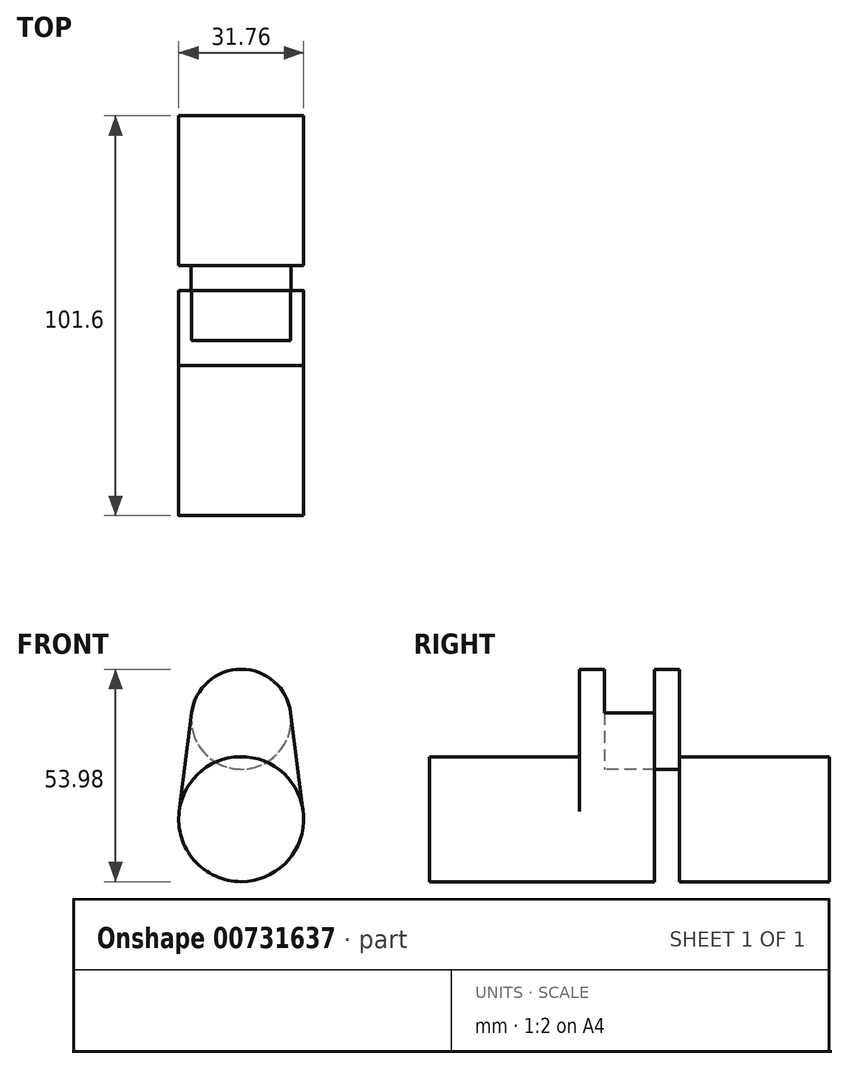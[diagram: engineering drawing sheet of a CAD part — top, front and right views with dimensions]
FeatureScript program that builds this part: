
annotation { "Feature Type Name" : "Feature", "Feature Type Description" : "" }
export const myFeature = defineFeature(function(context is Context, id is Id, definition is map)
    precondition{}
    {
        {
            var Q0;
            Q0=qCreatedBy(makeId("Front.planeOp"),FACE);
            var sketch = newSketch(context, id + "F0", { "sketchPlane" : qUnion([Q0])});
            skArc(sketch, "E0", {"start": v(-15.75, -10.72) * mm, "mid": v(0, -28.58) * mm, "end": v(15.75, -10.72) * mm});
            skArc(sketch, "E1", {"start": v(12.6, 14.29) * mm, "mid": v(0, 25.4) * mm, "end": v(-12.6, 14.29) * mm});
            skLineSegment(sketch, "E2", {"start": v(-12.6, 14.29) * mm, "end": v(-15.75, -10.72) * mm});
            skLineSegment(sketch, "E3", {"start": v(12.6, 14.29) * mm, "end": v(15.75, -10.72) * mm});
            skSolve(sketch);
        }
        {
            var Q0;
            Q0=makeQuery(id+"F0.imprint","IMPRINT",FACE,{"disambiguationData":[TD([[makeQuery(id+"F0.imprint","IMPRINT",EDGE,{"derivedFrom":sQuery(id+"F0.wireOp",EDGE,"E0")}),1.0]])]});
            extrude(context, id + "F1", {"entities" : qUnion([Q0]), "depth" : 6.35 * mm, "offsetDistance" : 25.4 * mm});
        }
        {
            var Q0;
            Q0=makeQuery(id+"F1.opExtrude","CAP_FACE",FACE,{"disambiguationData":[OSD([sQuery(id+"F0.wireOp",EDGE,"E0"),sQuery(id+"F0.wireOp",EDGE,"E1"),sQuery(id+"F0.wireOp",EDGE,"E2"),sQuery(id+"F0.wireOp",EDGE,"E3")])],"isStart":false});
            var sketch = newSketch(context, id + "F2", { "sketchPlane" : qUnion([Q0])});
            skCircle(sketch, "E4", {"center": v(0, -12.7) * mm, "radius": 15.88 * mm});
            skSolve(sketch);
        }
        {
            var Q0;
            {var subQ0=sQuery(id+"F2.wireOp",EDGE,"E4");var subQ1=makeQuery(id+"F2.imprint","INTERSECT",VERTEX,{"derivedFrom":[makeQuery(id+"F1.opExtrude","CAP_EDGE",EDGE,{"disambiguationData":[OSD([sQuery(id+"F0.wireOp",EDGE,"E2")])],"isStart":false}),subQ0]});Q0=makeQuery(id+"F2.imprint","IMPRINT",FACE,{"disambiguationData":[TD([[makeQuery(id+"F2.imprint","IMPRINT",EDGE,{"disambiguationData":[TD([[subQ1,-1.0]])],"derivedFrom":subQ0}),1.0]])]});}
            extrude(context, id + "F3", {"entities" : qUnion([Q0]), "operationType" : NewBodyOperationType.ADD, "depth" : 38.1 * mm, "offsetDistance" : 25.4 * mm});
        }
        {
            var Q0;
            Q0=makeQuery(id+"F1.opExtrude","CAP_FACE",FACE,{"disambiguationData":[OSD([sQuery(id+"F0.wireOp",EDGE,"E0"),sQuery(id+"F0.wireOp",EDGE,"E1"),sQuery(id+"F0.wireOp",EDGE,"E2"),sQuery(id+"F0.wireOp",EDGE,"E3")])],"isStart":true});
            var sketch = newSketch(context, id + "F4", { "sketchPlane" : qUnion([Q0])});
            skCircle(sketch, "E5", {"center": v(0, 12.7) * mm, "radius": 12.7 * mm});
            skSolve(sketch);
        }
        {
            var Q0;
            {var subQ0=sQuery(id+"F4.wireOp",EDGE,"E5");Q0=makeQuery(id+"F4.imprint","IMPRINT",FACE,{"disambiguationData":[TD([[makeQuery(id+"F4.imprint","IMPRINT",EDGE,{"disambiguationData":[OD(0.0)],"derivedFrom":subQ0}),-1.0]])]});}
            extrude(context, id + "F5", {"entities" : qUnion([Q0]), "operationType" : NewBodyOperationType.ADD, "depth" : 12.7 * mm, "offsetDistance" : 25.4 * mm});
        }
        {
            var Q0;
            Q0=makeQuery(id+"F5.opExtrude","CAP_FACE",FACE,{"disambiguationData":[OSD([sQuery(id+"F4.wireOp",EDGE,"E5")])],"isStart":false});
            var sketch = newSketch(context, id + "F6", { "sketchPlane" : qUnion([Q0])});
            skArc(sketch, "E6", {"start": v(12.6, 14.29) * mm, "mid": v(0, 25.4) * mm, "end": v(-12.6, 14.29) * mm});
            skArc(sketch, "E7", {"start": v(-15.75, -10.72) * mm, "mid": v(0, -28.58) * mm, "end": v(15.75, -10.72) * mm});
            skLineSegment(sketch, "E8", {"start": v(-12.6, 14.29) * mm, "end": v(-15.75, -10.72) * mm});
            skLineSegment(sketch, "E9", {"start": v(12.6, 14.29) * mm, "end": v(15.75, -10.72) * mm});
            skSolve(sketch);
        }
        {
            var Q0;
            Q0=makeQuery(id+"F6.imprint","IMPRINT",FACE,{"disambiguationData":[TD([[makeQuery(id+"F6.imprint","IMPRINT",EDGE,{"derivedFrom":sQuery(id+"F6.wireOp",EDGE,"E7")}),1.0]])]});
            var Q1;
            {var subQ0=sQuery(id+"F6.wireOp",EDGE,"E6");Q1=makeQuery(id+"F6.imprint","IMPRINT",FACE,{"disambiguationData":[TD([[makeQuery(id+"F6.imprint","IMPRINT",EDGE,{"derivedFrom":subQ0}),1.0]])]});}
            extrude(context, id + "F7", {"entities" : qUnion([Q0, Q1]), "operationType" : NewBodyOperationType.ADD, "depth" : 6.35 * mm, "offsetDistance" : 25.4 * mm});
        }
        {
            var Q0;
            Q0=makeQuery(id+"F7.opExtrude","CAP_FACE",FACE,{"disambiguationData":[OSD([sQuery(id+"F6.wireOp",EDGE,"E6"),sQuery(id+"F6.wireOp",EDGE,"E7"),sQuery(id+"F6.wireOp",EDGE,"E8"),sQuery(id+"F6.wireOp",EDGE,"E9")])],"isStart":false});
            var sketch = newSketch(context, id + "F8", { "sketchPlane" : qUnion([Q0])});
            skCircle(sketch, "E10", {"center": v(0, -12.7) * mm, "radius": 15.88 * mm});
            skSolve(sketch);
        }
        {
            var Q0;
            {var subQ0=sQuery(id+"F8.wireOp",EDGE,"E10");var subQ1=makeQuery(id+"F8.imprint","INTERSECT",VERTEX,{"derivedFrom":[makeQuery(id+"F7.opExtrude","CAP_EDGE",EDGE,{"disambiguationData":[OSD([sQuery(id+"F6.wireOp",EDGE,"E8")])],"isStart":false}),subQ0]});Q0=makeQuery(id+"F8.imprint","IMPRINT",FACE,{"disambiguationData":[TD([[makeQuery(id+"F8.imprint","IMPRINT",EDGE,{"disambiguationData":[TD([[subQ1,-1.0]])],"derivedFrom":subQ0}),1.0]])]});}
            extrude(context, id + "F9", {"entities" : qUnion([Q0]), "operationType" : NewBodyOperationType.ADD, "depth" : 38.1 * mm, "offsetDistance" : 25.4 * mm});
        }
    });
